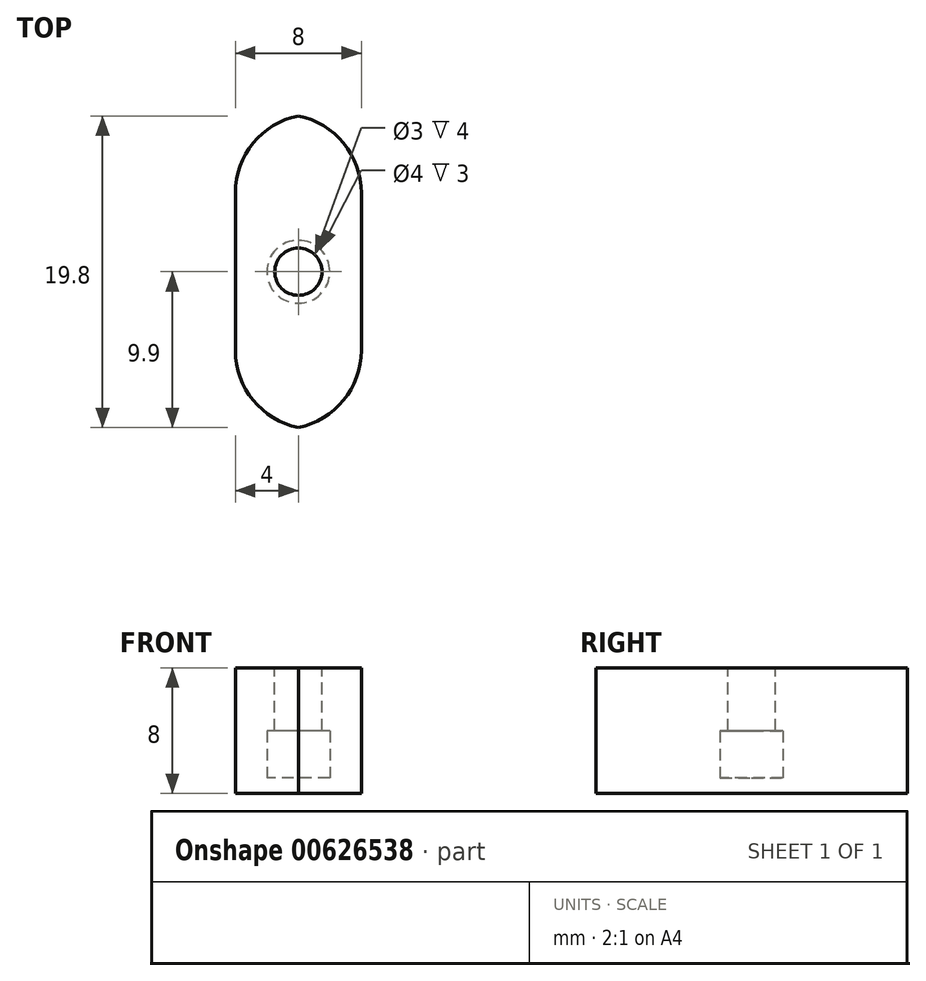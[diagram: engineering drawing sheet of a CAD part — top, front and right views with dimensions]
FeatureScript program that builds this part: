
annotation { "Feature Type Name" : "Feature", "Feature Type Description" : "" }
export const myFeature = defineFeature(function(context is Context, id is Id, definition is map)
    precondition{}
    {
        {
            var Q0;
            Q0=qCreatedBy(makeId("Top.planeOp"),FACE);
            var sketch = newSketch(context, id + "F0", { "sketchPlane" : qUnion([Q0])});
            skLineSegment(sketch, "E0.bottom", {"start": v(4, 10) * mm, "end": v(-4, 10) * mm});
            skLineSegment(sketch, "E0.top", {"start": v(4, -10) * mm, "end": v(-4, -10) * mm});
            skLineSegment(sketch, "E0.left", {"start": v(4, 10) * mm, "end": v(4, -10) * mm});
            skLineSegment(sketch, "E0.right", {"start": v(-4, 10) * mm, "end": v(-4, -10) * mm});
            skPoint(sketch, "E0.middle", {"position": v(0, 0) * mm});
            skSolve(sketch);
        }
        {
            var Q0;
            Q0=makeQuery(id+"F0.imprint","IMPRINT",FACE,{"disambiguationData":[TD([[makeQuery(id+"F0.imprint","IMPRINT",EDGE,{"derivedFrom":sQuery(id+"F0.wireOp",EDGE,"E0.bottom")}),1.0]])]});
            extrude(context, id + "F1", {"entities" : qUnion([Q0]), "depth" : 8 * mm, "offsetDistance" : 25 * mm});
        }
        {
            var Q0;
            Q0=makeQuery(id+"F1.opExtrude","SWEPT_EDGE",EDGE,{"disambiguationData":[OSD([sQuery(id+"F0.wireOp",EDGE,"E0.top"),sQuery(id+"F0.wireOp",EDGE,"E0.left")])]});
            var Q1;
            Q1=makeQuery(id+"F1.opExtrude","SWEPT_EDGE",EDGE,{"disambiguationData":[OSD([sQuery(id+"F0.wireOp",EDGE,"E0.top"),sQuery(id+"F0.wireOp",EDGE,"E0.right")])]});
            var Q2;
            Q2=makeQuery(id+"F1.opExtrude","SWEPT_EDGE",EDGE,{"disambiguationData":[OSD([sQuery(id+"F0.wireOp",EDGE,"E0.bottom"),sQuery(id+"F0.wireOp",EDGE,"E0.left")])]});
            var Q3;
            Q3=makeQuery(id+"F1.opExtrude","SWEPT_EDGE",EDGE,{"disambiguationData":[OSD([sQuery(id+"F0.wireOp",EDGE,"E0.bottom"),sQuery(id+"F0.wireOp",EDGE,"E0.right")])]});
            fillet(context, id + "F2", {"entities" : qUnion([Q0, Q1, Q2, Q3]), "radius" : 5 * mm, "tangentPropagation" : true, "allowEdgeOverflow" : false});
        }
        {
            var Q0;
            Q0=makeQuery(id+"F1.opExtrude","CAP_FACE",FACE,{"disambiguationData":[OSD([sQuery(id+"F0.wireOp",EDGE,"E0.bottom"),sQuery(id+"F0.wireOp",EDGE,"E0.top"),sQuery(id+"F0.wireOp",EDGE,"E0.left"),sQuery(id+"F0.wireOp",EDGE,"E0.right")])],"isStart":false});
            var sketch = newSketch(context, id + "F3", { "sketchPlane" : qUnion([Q0])});
            skCircle(sketch, "E1", {"center": v(0, 0) * mm, "radius": 1.5 * mm});
            skSolve(sketch);
        }
        {
            var Q0;
            Q0=makeQuery(id+"F3.imprint","IMPRINT",FACE,{"disambiguationData":[TD([[makeQuery(id+"F3.imprint","IMPRINT",EDGE,{"derivedFrom":sQuery(id+"F3.wireOp",EDGE,"E1")}),1.0]])]});
            extrude(context, id + "F4", {"entities" : qUnion([Q0]), "operationType" : NewBodyOperationType.REMOVE, "oppositeDirection" : true, "depth" : 7 * mm, "offsetDistance" : 25 * mm});
        }
        {
            var Q0;
            Q0=makeQuery(id+"F4.boolean.opBoolean","COPY",FACE,{"derivedFrom":makeQuery(id+"F4.opExtrude","CAP_FACE",FACE,{"disambiguationData":[OSD([sQuery(id+"F3.wireOp",EDGE,"E1")])],"isStart":false})});
            var sketch = newSketch(context, id + "F5", { "sketchPlane" : qUnion([Q0])});
            skCircle(sketch, "E2", {"center": v(0, 0) * mm, "radius": 2 * mm});
            skSolve(sketch);
        }
        {
            var Q0;
            Q0=makeQuery(id+"F5.imprint","IMPRINT",FACE,{"disambiguationData":[TD([[makeQuery(id+"F5.imprint","IMPRINT",EDGE,{"derivedFrom":sQuery(id+"F5.wireOp",EDGE,"E2")}),1.0]])]});
            extrude(context, id + "F6", {"entities" : qUnion([Q0]), "operationType" : NewBodyOperationType.REMOVE, "depth" : 3 * mm, "offsetDistance" : 25 * mm});
        }
    });
